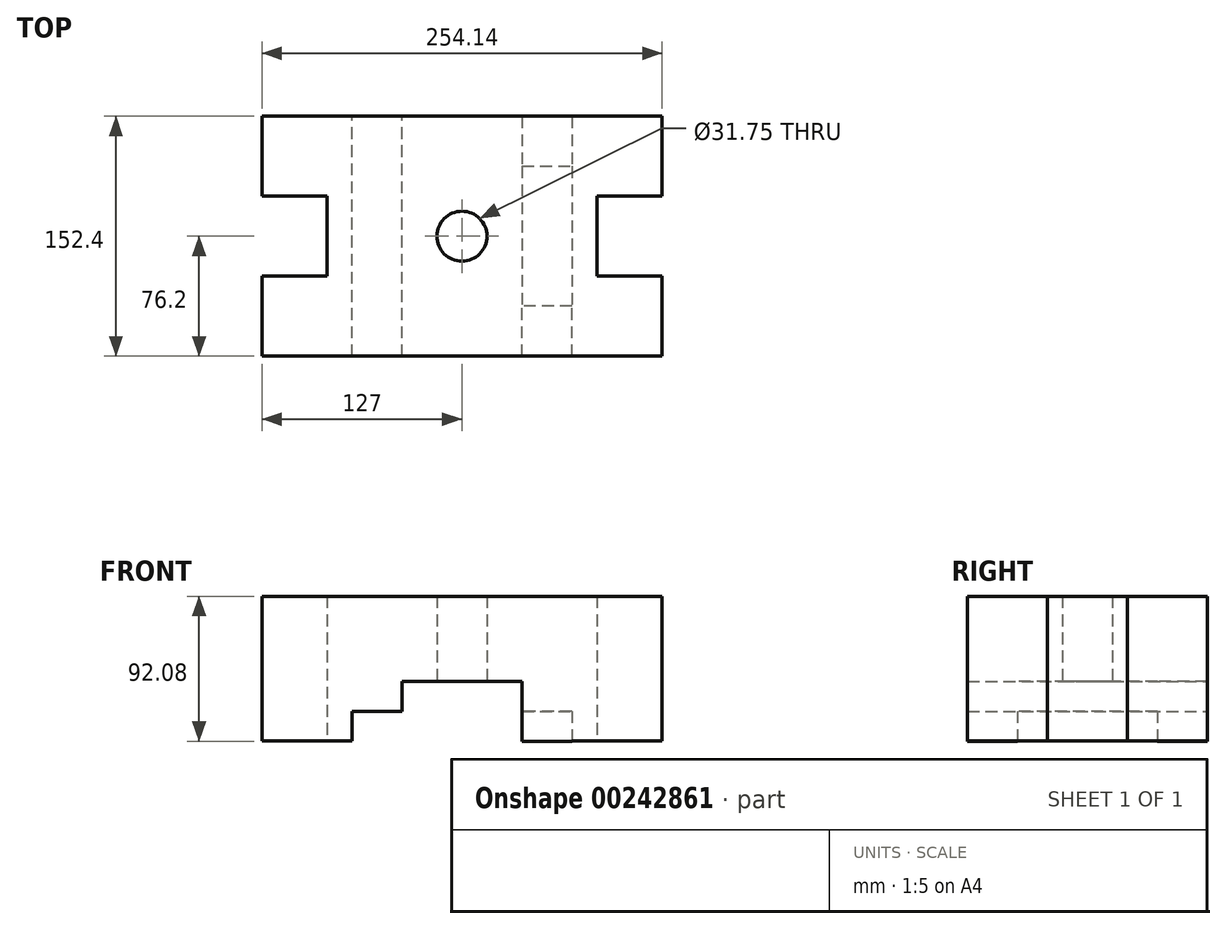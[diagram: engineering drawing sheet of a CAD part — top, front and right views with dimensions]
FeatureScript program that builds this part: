
annotation { "Feature Type Name" : "Feature", "Feature Type Description" : "" }
export const myFeature = defineFeature(function(context is Context, id is Id, definition is map)
    precondition{}
    {
        {
            var Q0;
            Q0=qCreatedBy(makeId("Top.planeOp"),FACE);
            var sketch = newSketch(context, id + "F0", { "sketchPlane" : qUnion([Q0])});
            skCircle(sketch, "E0", {"center": v(0, 0) * mm, "radius": 15.88 * mm});
            skLineSegment(sketch, "E1.bottom", {"start": v(-38.1, -76.2) * mm, "end": v(-69.85, -76.2) * mm});
            skLineSegment(sketch, "E1.top", {"start": v(-38.1, 76.2) * mm, "end": v(-69.85, 76.2) * mm});
            skLineSegment(sketch, "E1.left", {"start": v(-38.1, -76.2) * mm, "end": v(-38.1, 76.2) * mm});
            skLineSegment(sketch, "E1.right", {"start": v(-69.85, -76.2) * mm, "end": v(-69.85, 76.2) * mm});
            skLineSegment(sketch, "E2.bottom", {"start": v(69.85, -76.2) * mm, "end": v(38.1, -76.2) * mm});
            skLineSegment(sketch, "E2.top", {"start": v(69.85, -44.45) * mm, "end": v(38.1, -44.45) * mm});
            skLineSegment(sketch, "E2.left", {"start": v(69.85, -76.2) * mm, "end": v(69.85, -44.45) * mm});
            skLineSegment(sketch, "E2.right", {"start": v(38.1, -76.2) * mm, "end": v(38.1, -44.45) * mm});
            skLineSegment(sketch, "E3.top", {"start": v(38.24, 44.45) * mm, "end": v(69.99, 44.45) * mm});
            skLineSegment(sketch, "E3.left", {"start": v(38.24, 76.2) * mm, "end": v(38.24, 44.45) * mm});
            skLineSegment(sketch, "E3.right", {"start": v(69.99, 76.2) * mm, "end": v(69.99, 44.45) * mm});
            skLineSegment(sketch, "E4.top", {"start": v(-69.85, 44.45) * mm, "end": v(-38.1, 44.45) * mm});
            skLineSegment(sketch, "E4.left", {"start": v(-69.85, 76.2) * mm, "end": v(-69.85, 44.45) * mm});
            skLineSegment(sketch, "E4.right", {"start": v(-38.1, 76.56) * mm, "end": v(-38.1, 44.45) * mm});
            skLineSegment(sketch, "E5.top", {"start": v(-69.85, -44.45) * mm, "end": v(-38.1, -44.45) * mm});
            skLineSegment(sketch, "E5.left", {"start": v(-69.85, -76.2) * mm, "end": v(-69.85, -44.45) * mm});
            skLineSegment(sketch, "E6.right", {"start": v(127, -76.2) * mm, "end": v(127.05, -25.4) * mm});
            skLineSegment(sketch, "E7.right", {"start": v(-127, -76.2) * mm, "end": v(-127, -25.4) * mm});
            skLineSegment(sketch, "E8.bottom", {"start": v(-127, 25.4) * mm, "end": v(-85.72, 25.4) * mm});
            skLineSegment(sketch, "E8.top", {"start": v(-127, -25.4) * mm, "end": v(-85.72, -25.4) * mm});
            skLineSegment(sketch, "E8.right", {"start": v(-85.72, 25.4) * mm, "end": v(-85.72, -25.4) * mm});
            skLineSegment(sketch, "E9.bottom", {"start": v(127.1, 25.4) * mm, "end": v(85.82, 25.4) * mm});
            skLineSegment(sketch, "E9.top", {"start": v(127.1, -25.4) * mm, "end": v(85.82, -25.4) * mm});
            skLineSegment(sketch, "E9.right", {"start": v(85.82, 25.4) * mm, "end": v(85.82, -25.4) * mm});
            skLineSegment(sketch, "E10", {"start": v(-127, 76.2) * mm, "end": v(127.14, 76.2) * mm});
            skLineSegment(sketch, "E11", {"start": v(-127, -76.2) * mm, "end": v(127, -76.2) * mm});
            skLineSegment(sketch, "E12", {"start": v(69.99, 44.45) * mm, "end": v(69.85, -44.45) * mm});
            skLineSegment(sketch, "E13", {"start": v(38.24, 44.45) * mm, "end": v(38.1, -44.45) * mm});
            skLineSegment(sketch, "E14.trimOffspring", {"start": v(-127, 25.4) * mm, "end": v(-127, 76.2) * mm});
            skLineSegment(sketch, "E15.trimOffspring", {"start": v(127.1, 25.4) * mm, "end": v(127.14, 76.2) * mm});
            skSolve(sketch);
        }
        {
            var Q0;
            {var subQ1=sQuery(id+"F0.wireOp",EDGE,"E2.left");Q0=makeQuery(id+"F0.imprint","IMPRINT",FACE,{"disambiguationData":[TD([[makeQuery(id+"F0.imprint","IMPRINT",EDGE,{"derivedFrom":subQ1}),-1.0]])]});}
            var Q1;
            Q1=makeQuery(id+"F0.imprint","IMPRINT",FACE,{"disambiguationData":[TD([[makeQuery(id+"F0.imprint","IMPRINT",EDGE,{"derivedFrom":sQuery(id+"F0.wireOp",EDGE,"E1.right")}),1.0]])]});
            var Q2;
            Q2=makeQuery(id+"F0.imprint","IMPRINT",FACE,{"disambiguationData":[TD([[makeQuery(id+"F0.imprint","IMPRINT",EDGE,{"derivedFrom":sQuery(id+"F0.wireOp",EDGE,"E5.top")}),-1.0]])]});
            var Q3;
            Q3=makeQuery(id+"F0.imprint","IMPRINT",FACE,{"disambiguationData":[TD([[makeQuery(id+"F0.imprint","IMPRINT",EDGE,{"derivedFrom":sQuery(id+"F0.wireOp",EDGE,"E1.right")}),-1.0]])]});
            var Q4;
            {var subQ0=sQuery(id+"F0.wireOp",EDGE,"E4.top");Q4=makeQuery(id+"F0.imprint","IMPRINT",FACE,{"disambiguationData":[TD([[makeQuery(id+"F0.imprint","IMPRINT",EDGE,{"derivedFrom":subQ0}),1.0]])]});}
            var Q5;
            Q5=makeQuery(id+"F0.imprint","IMPRINT",FACE,{"disambiguationData":[TD([[makeQuery(id+"F0.imprint","IMPRINT",EDGE,{"derivedFrom":sQuery(id+"F0.wireOp",EDGE,"E2.top")}),-1.0]])]});
            var Q6;
            Q6=makeQuery(id+"F0.imprint","IMPRINT",FACE,{"disambiguationData":[TD([[makeQuery(id+"F0.imprint","IMPRINT",EDGE,{"derivedFrom":sQuery(id+"F0.wireOp",EDGE,"E0")}),-1.0]])]});
            var Q7;
            Q7=makeQuery(id+"F0.imprint","IMPRINT",FACE,{"disambiguationData":[TD([[makeQuery(id+"F0.imprint","IMPRINT",EDGE,{"derivedFrom":sQuery(id+"F0.wireOp",EDGE,"E2.top")}),1.0]])]});
            var Q8;
            Q8=makeQuery(id+"F0.imprint","IMPRINT",FACE,{"disambiguationData":[TD([[makeQuery(id+"F0.imprint","IMPRINT",EDGE,{"derivedFrom":sQuery(id+"F0.wireOp",EDGE,"E3.top")}),1.0]])]});
            extrude(context, id + "F1", {"entities" : qUnion([Q0, Q1, Q2, Q3, Q4, Q5, Q6, Q7, Q8]), "depth" : 92.07 * mm});
        }
        {
            var Q0;
            Q0=makeQuery(id+"F0.imprint","IMPRINT",FACE,{"disambiguationData":[TD([[makeQuery(id+"F0.imprint","IMPRINT",EDGE,{"derivedFrom":sQuery(id+"F0.wireOp",EDGE,"E1.right")}),1.0]])]});
            var Q1;
            {var subQ1=sQuery(id+"F0.wireOp",EDGE,"E2.left");Q1=makeQuery(id+"F0.imprint","IMPRINT",FACE,{"disambiguationData":[TD([[makeQuery(id+"F0.imprint","IMPRINT",EDGE,{"derivedFrom":subQ1}),-1.0]])]});}
            extrude(context, id + "F2", {"entities" : qUnion([Q0, Q1]), "operationType" : NewBodyOperationType.REMOVE, "depth" : 19 / 203.2 * mm});
        }
        {
            var Q0;
            Q0=makeQuery(id+"F0.imprint","IMPRINT",FACE,{"disambiguationData":[TD([[makeQuery(id+"F0.imprint","IMPRINT",EDGE,{"derivedFrom":sQuery(id+"F0.wireOp",EDGE,"E0")}),-1.0]])]});
            extrude(context, id + "F3", {"entities" : qUnion([Q0]), "operationType" : NewBodyOperationType.REMOVE, "depth" : 38.1 * mm});
        }
        {
            var Q0;
            Q0=makeQuery(id+"F0.imprint","IMPRINT",FACE,{"disambiguationData":[TD([[makeQuery(id+"F0.imprint","IMPRINT",EDGE,{"derivedFrom":sQuery(id+"F0.wireOp",EDGE,"E1.right")}),-1.0]])]});
            var Q1;
            Q1=makeQuery(id+"F0.imprint","IMPRINT",FACE,{"disambiguationData":[TD([[makeQuery(id+"F0.imprint","IMPRINT",EDGE,{"derivedFrom":sQuery(id+"F0.wireOp",EDGE,"E2.top")}),-1.0]])]});
            extrude(context, id + "F4", {"entities" : qUnion([Q0, Q1]), "operationType" : NewBodyOperationType.REMOVE, "depth" : 19.05 * mm});
        }
    });
